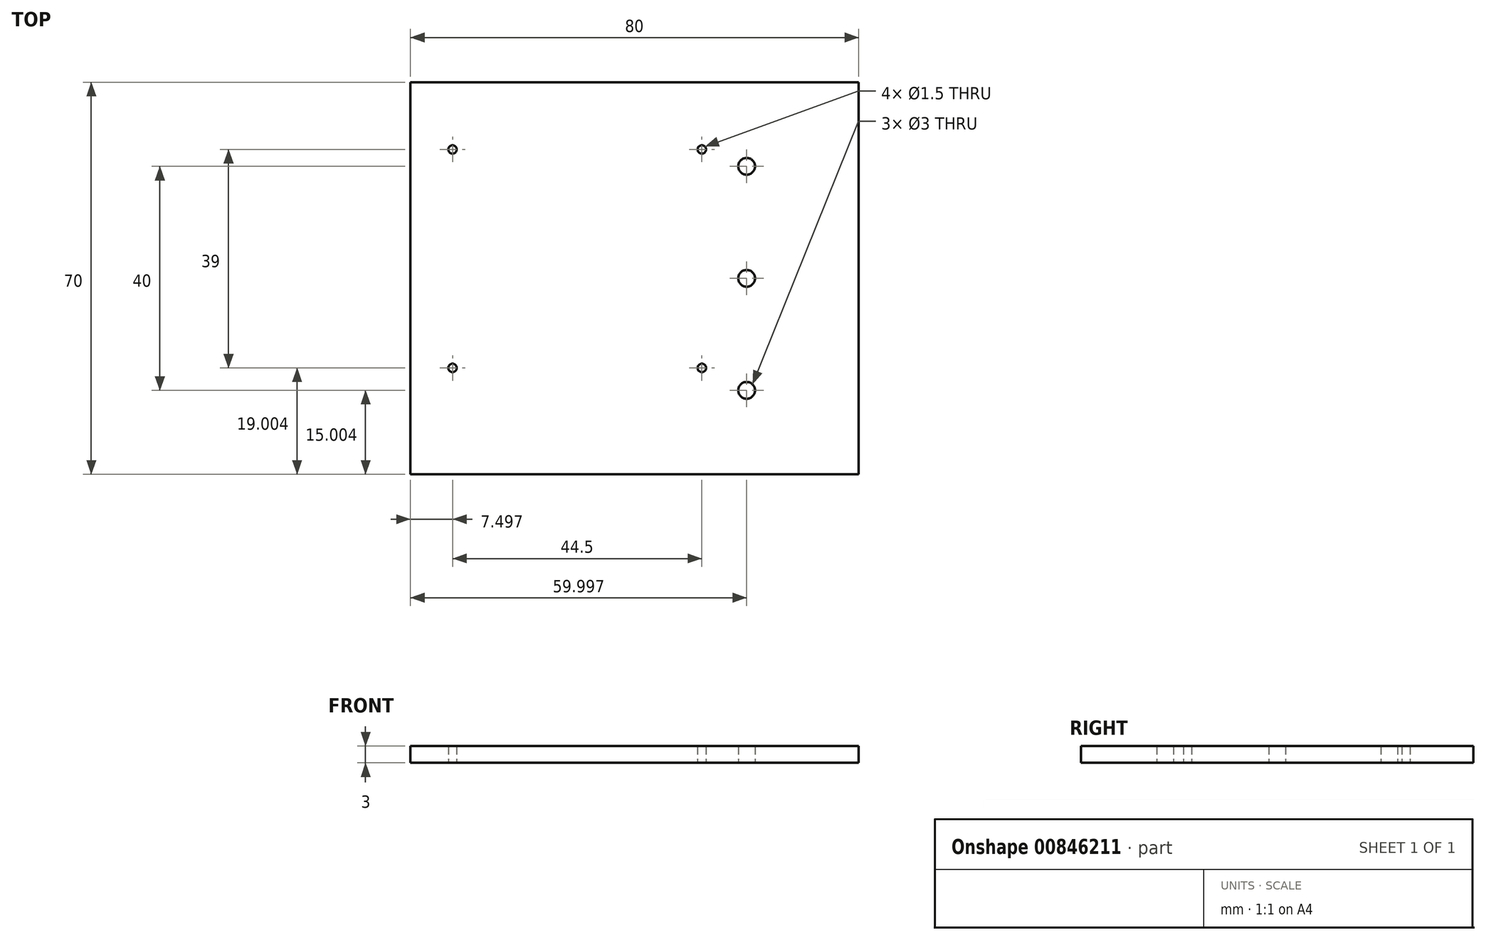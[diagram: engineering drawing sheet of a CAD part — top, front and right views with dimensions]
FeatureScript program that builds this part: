
annotation { "Feature Type Name" : "Feature", "Feature Type Description" : "" }
export const myFeature = defineFeature(function(context is Context, id is Id, definition is map)
    precondition{}
    {
        {
            var Q0;
            Q0=qCreatedBy(makeId("Top.planeOp"),FACE);
            var sketch = newSketch(context, id + "F0", { "sketchPlane" : qUnion([Q0])});
            skLineSegment(sketch, "E0.bottom", {"start": v(-15.81, 33.5) * mm, "end": v(64.19, 33.5) * mm});
            skLineSegment(sketch, "E0.top", {"start": v(-15.81, -36.5) * mm, "end": v(64.19, -36.5) * mm});
            skLineSegment(sketch, "E0.left", {"start": v(-15.81, 33.5) * mm, "end": v(-15.81, -36.5) * mm});
            skLineSegment(sketch, "E0.right", {"start": v(64.19, 33.5) * mm, "end": v(64.19, -36.5) * mm});
            skLineSegment(sketch, "E1", {"start": v(-6.81, 33.5) * mm, "end": v(44.19, 33.5) * mm});
            skLineSegment(sketch, "E2", {"start": v(44.19, 33.5) * mm, "end": v(44.19, 18.5) * mm});
            skLineSegment(sketch, "E3", {"start": v(44.19, 18.5) * mm, "end": v(44.19, -1.5) * mm});
            skLineSegment(sketch, "E4", {"start": v(44.19, -1.5) * mm, "end": v(44.19, -21.5) * mm});
            skCircle(sketch, "E5", {"center": v(44.19, 18.5) * mm, "radius": 1.5 * mm});
            skCircle(sketch, "E6", {"center": v(44.19, -1.5) * mm, "radius": 1.5 * mm});
            skCircle(sketch, "E7", {"center": v(44.19, -21.5) * mm, "radius": 1.5 * mm});
            skLineSegment(sketch, "E8", {"start": v(-15.81, 33.5) * mm, "end": v(-10.81, 33.5) * mm});
            skLineSegment(sketch, "E9", {"start": v(-10.81, 33.5) * mm, "end": v(-8.31, 33.5) * mm});
            skLineSegment(sketch, "E10", {"start": v(-8.31, 33.5) * mm, "end": v(-8.31, 21.5) * mm});
            skLineSegment(sketch, "E11", {"start": v(-8.31, 21.5) * mm, "end": v(36.19, 21.5) * mm});
            skLineSegment(sketch, "E12", {"start": v(36.19, 21.5) * mm, "end": v(36.19, -17.5) * mm});
            skLineSegment(sketch, "E13", {"start": v(36.19, -17.5) * mm, "end": v(-8.31, -17.5) * mm});
            skCircle(sketch, "E14", {"center": v(-8.31, 21.5) * mm, "radius": 0.75 * mm});
            skCircle(sketch, "E15", {"center": v(36.19, 21.5) * mm, "radius": 0.75 * mm});
            skCircle(sketch, "E16", {"center": v(36.19, -17.5) * mm, "radius": 0.75 * mm});
            skCircle(sketch, "E17", {"center": v(-8.31, -17.5) * mm, "radius": 0.75 * mm});
            skSolve(sketch);
        }
        {
            var Q0;
            {var subQ0=sQuery(id+"F0.wireOp",EDGE,"E0.left");Q0=makeQuery(id+"F0.imprint","IMPRINT",FACE,{"disambiguationData":[TD([[makeQuery(id+"F0.imprint","IMPRINT",EDGE,{"derivedFrom":subQ0}),1.0]])]});}
            var Q1;
            Q1=makeQuery(id+"F0.imprint","IMPRINT",FACE,{"disambiguationData":[TD([[makeQuery(id+"F0.imprint","IMPRINT",EDGE,{"derivedFrom":sQuery(id+"F0.wireOp",EDGE,"E0.bottom")}),-1.0]])]});
            extrude(context, id + "F1", {"entities" : qUnion([Q0, Q1]), "depth" : 3 * mm, "offsetDistance" : 25 * mm});
        }
    });
